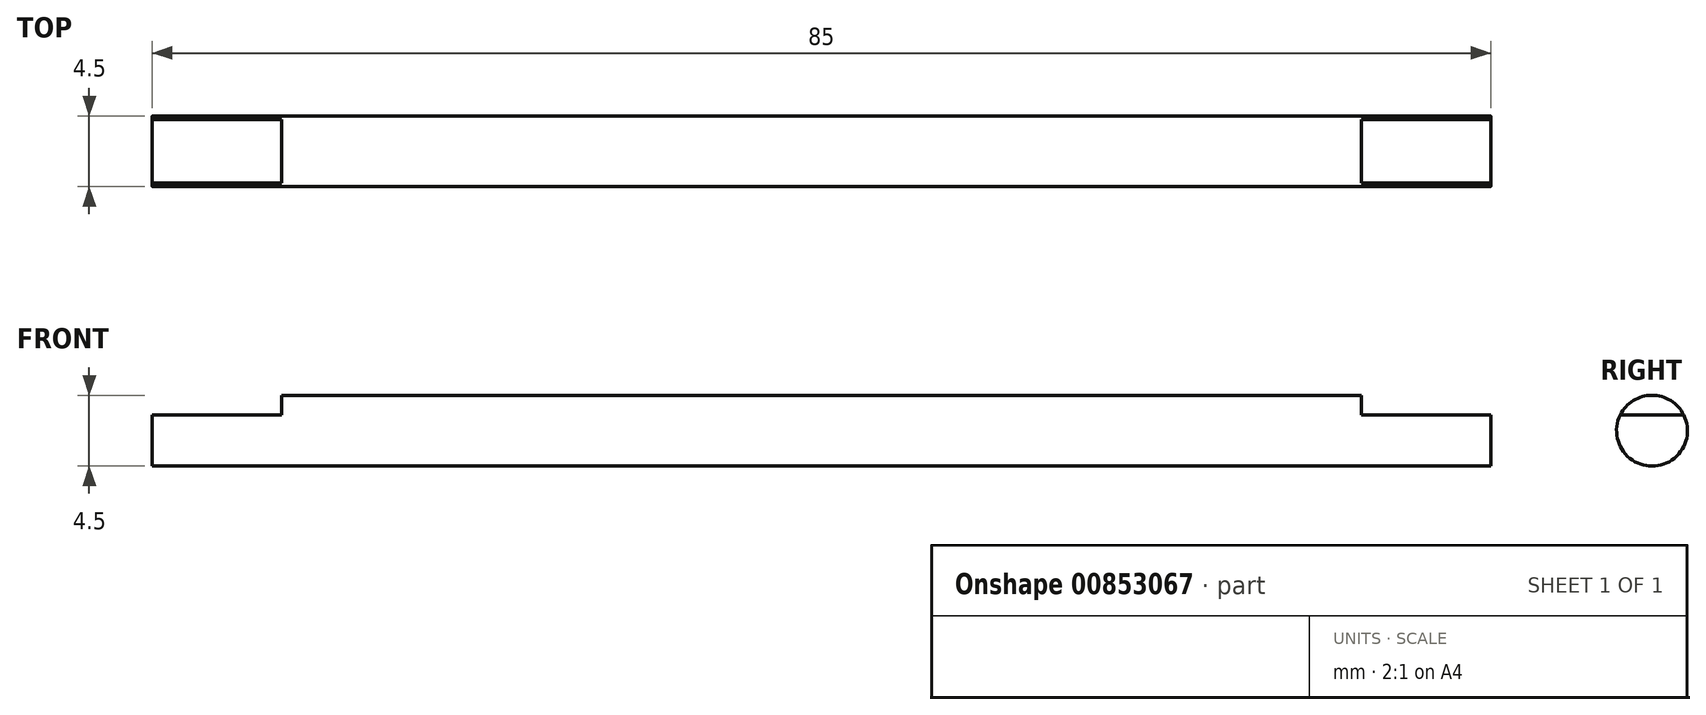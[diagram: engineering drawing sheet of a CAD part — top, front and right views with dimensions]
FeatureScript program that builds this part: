
annotation { "Feature Type Name" : "Feature", "Feature Type Description" : "" }
export const myFeature = defineFeature(function(context is Context, id is Id, definition is map)
    precondition{}
    {
        {
            var Q0;
            Q0=qCreatedBy(makeId("Right.planeOp"),FACE);
            var sketch = newSketch(context, id + "F0", { "sketchPlane" : qUnion([Q0])});
            skCircle(sketch, "E0", {"center": v(0, 0) * mm, "radius": 2.25 * mm});
            skSolve(sketch);
        }
        {
            var Q0;
            Q0 = qSketchRegion(id + "F0", true);
            extrude(context, id + "F1", {"entities" : qUnion([Q0]), "depth" : 85 * mm, "offsetDistance" : 25 * mm});
        }
        {
            var Q0;
            Q0=qCreatedBy(makeId("Top.planeOp"),FACE);
            cPlane(context, id + "F2", {"entities" : qUnion([Q0]), "cplaneType" : CPlaneType.OFFSET, "offset" : 1 * mm, "width" : 150 * mm, "height" : 150 * mm});
        }
        {
            var Q0;
            Q0=qCreatedBy(id+"F2.planeOp",FACE);
            var sketch = newSketch(context, id + "F3", { "sketchPlane" : qUnion([Q0])});
            skLineSegment(sketch, "E1.bottom", {"start": v(0, 8.88) * mm, "end": v(8.2, 8.88) * mm});
            skLineSegment(sketch, "E1.top", {"start": v(0, -9.1) * mm, "end": v(8.2, -9.1) * mm});
            skLineSegment(sketch, "E1.left", {"start": v(0, 8.88) * mm, "end": v(0, -9.1) * mm});
            skLineSegment(sketch, "E1.right", {"start": v(8.2, 8.88) * mm, "end": v(8.2, -9.1) * mm});
            skLineSegment(sketch, "E2.bottom", {"start": v(76.8, 10.3) * mm, "end": v(85, 10.3) * mm});
            skLineSegment(sketch, "E2.top", {"start": v(76.8, -10.43) * mm, "end": v(85, -10.43) * mm});
            skLineSegment(sketch, "E2.left", {"start": v(76.8, 10.3) * mm, "end": v(76.8, -10.43) * mm});
            skLineSegment(sketch, "E2.right", {"start": v(85, 10.3) * mm, "end": v(85, -10.43) * mm});
            skSolve(sketch);
        }
        {
            var Q0;
            Q0 = qSketchRegion(id + "F3", true);
            extrude(context, id + "F4", {"entities" : qUnion([Q0]), "operationType" : NewBodyOperationType.REMOVE, "depth" : 25 * mm, "offsetDistance" : 25 * mm});
        }
    });
